# Revit family: Sanitary_Toilets_DURAVIT-AG_Starck-3-Toilet-wall-mounted-Duravit-Rim 452709_NEW
name_source: partatom
category: Plumbing Fixtures
revit_build: Autodesk Revit 2018 (Build: 20170223_1515(x64)
units: mm (PartAtom-declared; Revit-internal decimal feet)

## family parameters
Cut with Voids When Loaded = No
Host = Face
OmniClass Number = 23.31.19.00
OmniClass Title = Toilets
Part Type = Normal
Room Calculation Point = No
Round Connector Dimension = Use Diameter
Shared = No

## types (2) — shared parameters
Always visible = Yes
Connector Description = Water Inlet 55 mm
Default Elevation = 1219 mm
Depth = 540 mm  [stored 1.77165 ft]
Description = Packaging dimensions 560 x 400 x 450 mm
Diameter = 55  [stored 0.180446 ft]
Edition number = 1
Height = 425 mm  [stored 1.39436 ft]
IFC Classification = Sanitary Terminal
Installation instructions = http://pro.duravit.com
Manufacturer = Duravit
Manufacturer name = DURAVIT AG
Masterformat 2014 Code = 01 52 19
Masterformat 2014 Description = Sanitary Facilities
Material 1 = Duravit - Ceramic - 00 - White Alpin
Material 2 = Duravit - Metal - Chrome
Material main = Ceramics
Model = Starck 3 Toilet wall mounted Duravit Rimless¨ set 452709
NBS Reference Code = 35-65-90
NBS Reference Description = Toilet Systems
OmniClass Code = 23-31 19 00
OmniClass Description = Toilets
Outlet Connector Description = Sanitary outlet 102 mm
Outlet Diameter = 102
Product Guid = 2b043d5e-4d61-4538-9666-492cdee1b503
Product SKU = starck-3-toilet-wall-mounted-duravit-rimless-set-452709
Product certification = http://pro.duravit.com
Product data url = https://bimobject.com
Product name = Starck 3 Toilet wall mounted Duravit Rimless¨ set 452709
Product url = http://pro.duravit.com
QR code = https://bimobject.com
Technical description = http://pro.duravit.com
UNSPSC Code = 301815
URL = http://pro.duravit.com
Uniclass 1.4 Code = L7216
Uniclass 1.4 Description = Toilets
Uniclass 2.0 Code = SS-35-65-90
Uniclass 2.0 Description = Toilet Systems
Uniclass 2015 Code = Pr_40_20_93
Uniclass 2015 Name = Urinal and WC fittings
Uniformat II Code = D2030
Uniformat II Description = Sanitary Waste
Weight = 29.40 kg
Width = 370 mm  [stored 1.21391 ft]

## type names (no varying parameters)
- Starck 3 Toilet wall mounted Duravit Rimless set - 45270900A1
- Starck 3 Toilet wall mounted Duravit Rimless set - 45270900A11

note: [stored X ft] marks values corroborated as IEEE doubles in the binary element streams (Revit-internal decimal feet)

## geometry (parser evidence)
native form markers: Sweep x4
no freeform markers — native parametric forms only
